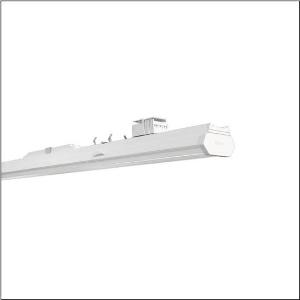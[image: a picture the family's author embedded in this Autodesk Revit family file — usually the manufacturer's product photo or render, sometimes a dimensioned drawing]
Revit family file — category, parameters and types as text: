
# Revit family: licross_r__11_protected_ho_51td1bmn4fxm_4fca
name_source: partatom
category: Lighting Fixtures
units: mm (PartAtom-declared; Revit-internal decimal feet)

## family parameters
Cut with Voids When Loaded = No
Host = Face
Light Source = No
Part Type = Normal
Room Calculation Point = No
Round Connector Dimension = Use Diameter
Shared = No

## types (1)
- --- (1 x LED, 15020 lm, 87.4 W, 4000K)
    Apparent Load = 87 VA
    CIE Flux Codes = 54 82 95 97 100
    Color Rendering = 80
    Color Temperature = 4000K
    Default Elevation = 1800 mm
    Description = Licross® 11 Protected HO, luminaire insert, of sheet steel, galvanised, coil coated, white, length: 1.500mm, width: 90mm, height: 101mm, LED rated luminous flux: 15.020lm, light colour: 840, control gear: ON/OFF Multilumen, with plug, 3-pole, with phase selection, mains connection: 220..240V, AC, 50/60Hz, rated input power: 87W, halogen-free wiring, primary optical cover: cover, of PMMA, light emission: direct distribution, primary light characteristic: symmetric, protection rating (complete): IP54, insulation class (complete): insulation class I (protective earthing), certification: CE, ENEC, VDE, UKCA, protection symbol: D if used in an environment with non-conductive dust loads with corresponding accessories, impact resistance: IK06, permissible ambient temperature for indoor applications: -35..+35°C, corresponds to IFS (International Featured Standards) requirements for safety and quality in the food industry, reducing of maximum allowable ambient temperature of 5°C with ceiling mounting, LABS conformity tested according to VDMA 24364:2018-05, packaging unit: 1 piece
    Height = 92 mm
    Lamp = 1 x LED
    Lamp Light Flux = 15020 lm
    Lamp Power = 87.4 W
    Lamp count = 1
    Length = 1500 mm
    Luminous efficacy = 172 lm/W
    Manufacturer = Siteco
    ModVariant = No
    Model = 51TD1BMN4FXM
    Mounting Place = Ceiling
    Mounting Type = Pendant
    Number of Poles = 1
    OnlyDefault = Yes
    Power Factor = 1
    Product Name = Licross® 11 Protected HO
    Product group = luminaire insert
    ProductGroupID = 901
    Protection Class = Protection class I
    Protection Degree = IP 54
    RLX_Detail_Level = 1
    RLX_Emergency_Light_Flux = 0 lm
    RLX_Emergency_Type = 0
    RLX_Emergency_Type_DB = No
    RlxData = <blob elided: 21989 chars, md5=19c3d7a2>
    Socket = socket
    Standby Power = 0 W
    System Light Flux = 15020 lm
    System Power = 87 W
    Type Comments = factory setting: luminous flux: 100 % | (A | C | E) | 203 mA
    Type Image = l_1256145.jpg
    URL = http://relux.com
    VarID = @adj_055417
    Voltage = 0 V
    Weight = 0.00 kg
    Width = 88 mm

## geometry (parser evidence)
native form markers: Blend x4, Sweep x10
no freeform markers — native parametric forms only
